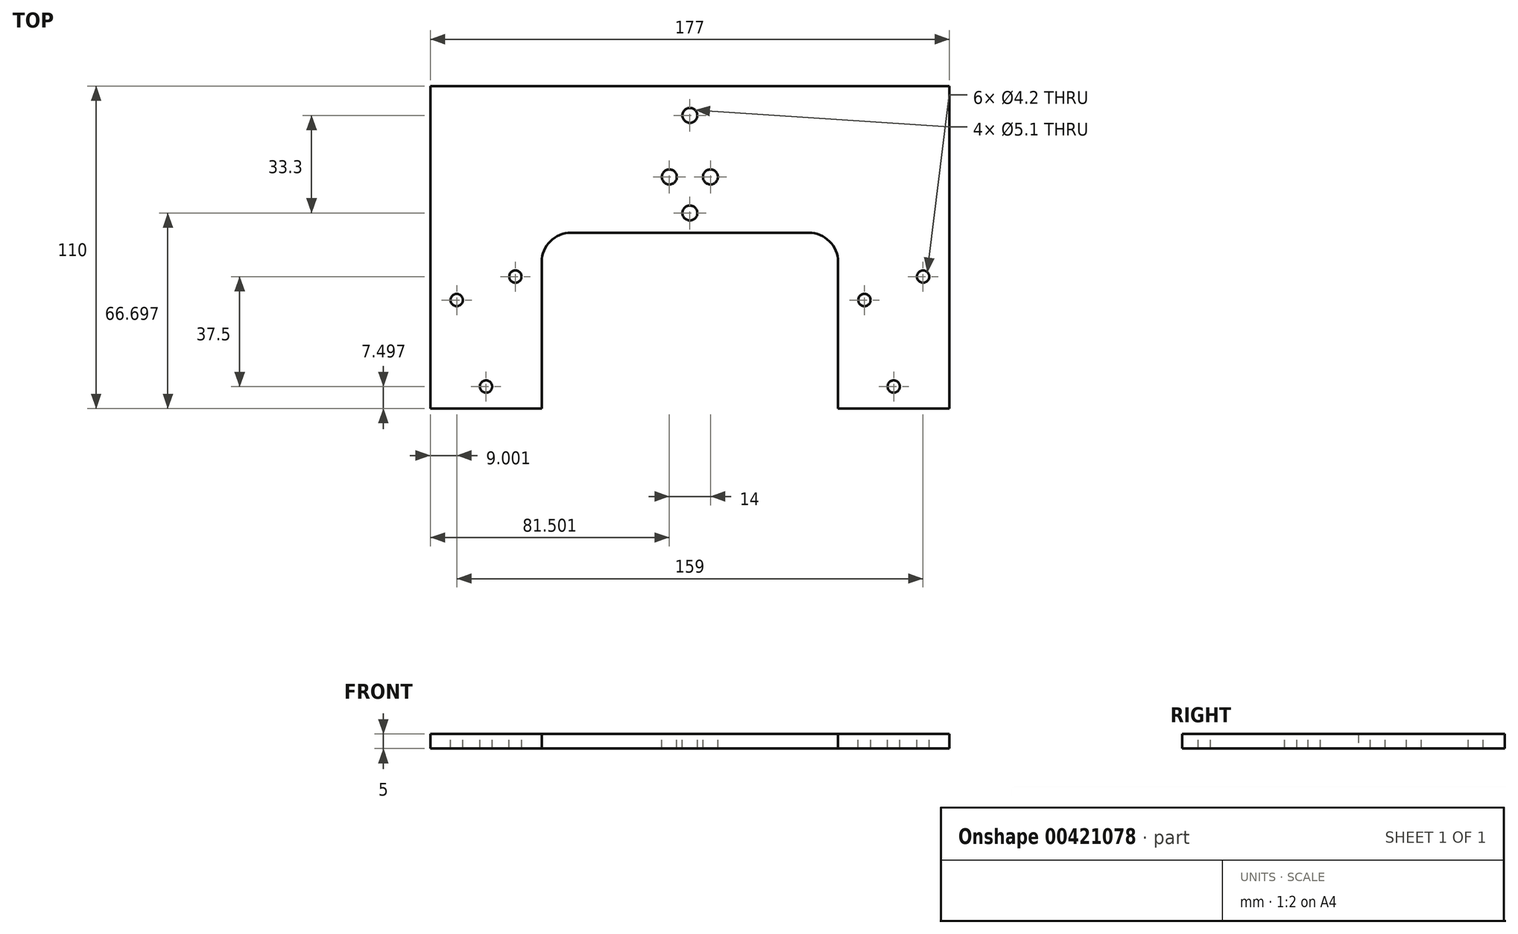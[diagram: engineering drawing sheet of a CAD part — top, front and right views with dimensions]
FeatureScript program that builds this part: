
annotation { "Feature Type Name" : "Feature", "Feature Type Description" : "" }
export const myFeature = defineFeature(function(context is Context, id is Id, definition is map)
    precondition{}
    {
        {
            var Q0;
            Q0=qCreatedBy(makeId("Top.planeOp"),FACE);
            var sketch = newSketch(context, id + "F0", { "sketchPlane" : qUnion([Q0])});
            skLineSegment(sketch, "E0.bottom", {"start": v(-92.32, 58.53) * mm, "end": v(84.68, 58.53) * mm});
            skLineSegment(sketch, "E0.top", {"start": v(-44.32, 8.53) * mm, "end": v(36.68, 8.53) * mm});
            skLineSegment(sketch, "E0.left", {"start": v(-92.32, 58.53) * mm, "end": v(-92.32, 8.53) * mm});
            skLineSegment(sketch, "E0.right", {"start": v(84.68, 58.53) * mm, "end": v(84.68, 8.53) * mm});
            skLineSegment(sketch, "E1.top", {"start": v(-92.32, -51.47) * mm, "end": v(-54.32, -51.47) * mm});
            skLineSegment(sketch, "E1.left", {"start": v(-92.32, 8.53) * mm, "end": v(-92.32, -51.47) * mm});
            skLineSegment(sketch, "E1.right", {"start": v(-54.32, -1.47) * mm, "end": v(-54.32, -51.47) * mm});
            skLineSegment(sketch, "E2.top", {"start": v(84.68, -51.47) * mm, "end": v(46.68, -51.47) * mm});
            skLineSegment(sketch, "E2.left", {"start": v(84.68, 8.53) * mm, "end": v(84.68, -51.47) * mm});
            skLineSegment(sketch, "E2.right", {"start": v(46.68, -1.47) * mm, "end": v(46.68, -51.47) * mm});
            skPoint(sketch, "E3.visualSharp", {"position": v(-54.32, 8.53) * mm});
            skArc(sketch, "E3.filletArc", {"start": v(-44.32, 8.53) * mm, "mid": v(-51.39, 5.6) * mm, "end": v(-54.32, -1.47) * mm});
            skPoint(sketch, "E4.visualSharp", {"position": v(46.68, 8.53) * mm});
            skArc(sketch, "E4.filletArc", {"start": v(46.68, -1.47) * mm, "mid": v(43.75, 5.6) * mm, "end": v(36.68, 8.53) * mm});
            skSolve(sketch);
        }
        {
            var Q0;
            Q0=qSketchRegion(id+"F0",true);
            extrude(context, id + "F1", {"entities" : qUnion([Q0]), "depth" : 5 * mm});
        }
        {
            var Q0;
            Q0=makeQuery(id+"F1.opExtrude","CAP_FACE",FACE,{"disambiguationData":[OSD([sQuery(id+"F0.wireOp",EDGE,"E0.bottom"),sQuery(id+"F0.wireOp",EDGE,"E0.top"),sQuery(id+"F0.wireOp",EDGE,"E0.left"),sQuery(id+"F0.wireOp",EDGE,"E0.right")])],"isStart":false});
            var sketch = newSketch(context, id + "F2", { "sketchPlane" : qUnion([Q0])});
            skPoint(sketch, "E5", {"position": v(-3.82, 48.53) * mm});
            skPoint(sketch, "E6", {"position": v(-3.82, 15.23) * mm});
            skPoint(sketch, "E7", {"position": v(-10.82, 27.53) * mm});
            skPoint(sketch, "E8", {"position": v(3.18, 27.53) * mm});
            skSolve(sketch);
        }
        {
            var Q0;
            Q0=sQuery(id+"F2.wireOp",VERTEX,"E7");
            var Q1;
            Q1=sQuery(id+"F2.wireOp",VERTEX,"E5");
            var Q2;
            Q2=sQuery(id+"F2.wireOp",VERTEX,"E8");
            var Q3;
            Q3=sQuery(id+"F2.wireOp",VERTEX,"E6");
            var Q4;
            Q4=makeQuery(id+"F1.opExtrude","SWEPT_BODY",BODY,{"disambiguationData":[OSD([sQuery(id+"F0.wireOp",EDGE,"E0.bottom"),sQuery(id+"F0.wireOp",EDGE,"E0.top"),sQuery(id+"F0.wireOp",EDGE,"E0.left"),sQuery(id+"F0.wireOp",EDGE,"E0.right")])]});
            hole(context, id + "F3", {"style" : HoleStyle.SIMPLE, "endStyle" : HoleEndStyle.THROUGH, "standardTappedOrClearance" : lookupTablePath({ "standard" : "ISO", "size" : "5.1", "type" : "Drilled" }), "standardBlindInLast" : lookupTablePath({ "standard" : "ISO", "size" : "5.1", "type" : "Drilled" }), "holeDiameter" : 5.1 * mm, "tappedDepth" : 12.7 * mm, "tapClearance" : 3, "locations" : qUnion([Q0, Q1, Q2, Q3]), "scope" : qUnion([Q4])});
        }
        {
            var Q0;
            Q0=makeQuery(id+"F1.opExtrude","CAP_FACE",FACE,{"disambiguationData":[OSD([sQuery(id+"F0.wireOp",EDGE,"E0.bottom"),sQuery(id+"F0.wireOp",EDGE,"E0.top"),sQuery(id+"F0.wireOp",EDGE,"E0.left"),sQuery(id+"F0.wireOp",EDGE,"E0.right"),sQuery(id+"F0.wireOp",EDGE,"E1.top"),sQuery(id+"F0.wireOp",EDGE,"E1.left"),sQuery(id+"F0.wireOp",EDGE,"E1.right"),sQuery(id+"F0.wireOp",EDGE,"E2.top"),sQuery(id+"F0.wireOp",EDGE,"E2.left"),sQuery(id+"F0.wireOp",EDGE,"E2.right"),sQuery(id+"F0.wireOp",EDGE,"E3.filletArc"),sQuery(id+"F0.wireOp",EDGE,"E4.filletArc")])],"isStart":false});
            var sketch = newSketch(context, id + "F4", { "sketchPlane" : qUnion([Q0])});
            skPoint(sketch, "E9", {"position": v(-73.32, -43.97) * mm});
            skPoint(sketch, "E10", {"position": v(65.68, -43.97) * mm});
            skPoint(sketch, "E11", {"position": v(-83.32, -14.47) * mm});
            skPoint(sketch, "E12", {"position": v(75.68, -6.47) * mm});
            skCircle(sketch, "E13", {"center": v(-63.32, -6.47) * mm, "radius": 2.1 * mm});
            skCircle(sketch, "E14", {"center": v(55.68, -14.47) * mm, "radius": 2.1 * mm});
            skCircle(sketch, "E15", {"center": v(-83.32, -14.47) * mm, "radius": 2.1 * mm});
            skCircle(sketch, "E16", {"center": v(-73.32, -43.97) * mm, "radius": 2.1 * mm});
            skCircle(sketch, "E17", {"center": v(75.68, -6.47) * mm, "radius": 2.1 * mm});
            skCircle(sketch, "E18", {"center": v(65.68, -43.97) * mm, "radius": 2.1 * mm});
            skSolve(sketch);
        }
        {
            var Q0;
            Q0 = qSketchRegion(id + "F4", true);
            extrude(context, id + "F5", {"entities" : qUnion([Q0]), "operationType" : NewBodyOperationType.REMOVE, "oppositeDirection" : true, "depth" : 25 * mm});
        }
    });
